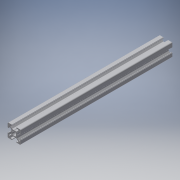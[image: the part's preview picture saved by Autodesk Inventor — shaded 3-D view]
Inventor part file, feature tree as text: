
AUTODESK INVENTOR PART (.ipt)
format: ipt  version: 2016 (Build 200138000, 138)  size: 313,344 bytes
history: native  units: in
note: dims shown in document units (in); Inventor stores cm internally (conversion verified against a paired STEP export)
features: other x3, extrude x1, sketch x1
ambient origin geometry x8: Origin, YZ Plane, XZ Plane, XY Plane, X Axis, Y Axis, Z Axis, Center Point
bodies: Solid1 (feature_tree)
feature tree (5):
  other  "Blocks"
  extrude  "Extrusion1"  [1 undecoded]
  sketch  "Sketch1"  dims[d1=0.0in]
  other  "20x20"
  other  "20x20:1"
note: 1 required parameter value undecoded (feature->parameter linkage not recoverable at this tier; creation-order binding heuristic only, values carry confidence <= 0.55)
